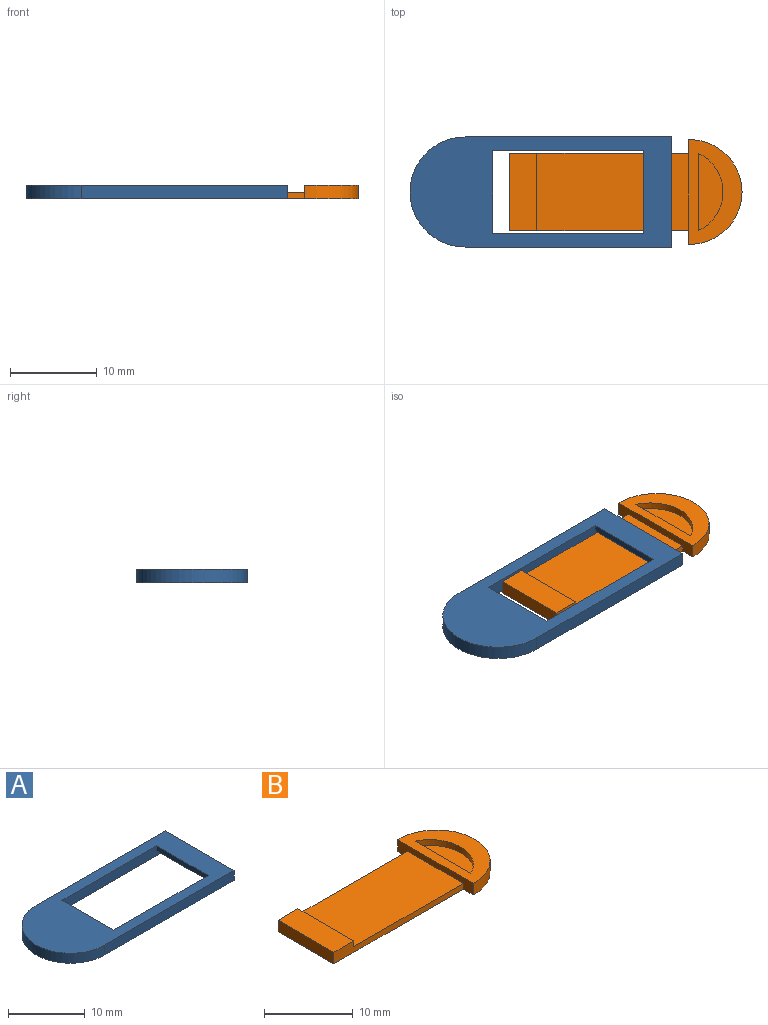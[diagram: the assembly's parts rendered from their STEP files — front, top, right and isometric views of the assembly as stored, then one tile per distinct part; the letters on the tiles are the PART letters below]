
ASSEMBLY  parts=2 mates=1
PART A: 11 faces, bbox 30.2x12.7x1.6 mm
  f0: plane 9.53x0.79mm, normal (-1,0,0), area 7.6mm2, adj f3,f7,f8,f10
  f1: plane 12.7x1.59mm, normal (1,0,0), area 12.6mm2, adj f3,f5,f6,f7,f8,f9,f10
  f2: plane 9.53x1.59mm, normal (1,0,0), area 15.1mm2, adj f3,f7,f8,f9
  f3: plane 20.64x1.59mm, normal (0,-1,0), area 30.2mm2, adj f0,f1,f2,f8,f9,f10
  f4: cylinder r=6.35mm len=12.7mm, axis (0,0,-1), area 31.7mm2, adj f5,f6,f8,f9
  f5: plane 23.81x1.59mm, normal (0,-1,0), area 37.8mm2, adj f1,f4,f8,f9
  f6: plane 23.81x1.59mm, normal (0,1,0), area 37.8mm2, adj f1,f4,f8,f9
  f7: plane 20.64x1.59mm, normal (0,1,0), area 30.2mm2, adj f0,f1,f2,f8,f9,f10
  f8: plane 30.16x12.7mm, normal (0,0,1), area 199.4mm2, adj f0,f1,f2,f3,f4,f5,f6,f7
  f9: plane 30.16x12.7mm, normal (0,0,-1), area 169.2mm2, adj f1,f2,f3,f4,f5,f6,f7
  f10: plane 9.53x3.18mm, normal (0,0,-1), area 30.2mm2, adj f0,f1,f3,f7
PART B: 13 faces, bbox 26.8x12.1x1.6 mm
  f0: plane 20.64x1.59mm, normal (0,1,0), area 18.9mm2, adj f1,f3,f6,f7,f11,f12
  f1: plane 8.89x3.18mm, normal (0,0,1), area 28.2mm2, adj f0,f3,f4,f11
  f2: plane 12.07x6.21mm, normal (0,0,1), area 41.3mm2, adj f5,f6,f8,f9
  f3: plane 8.89x1.59mm, normal (-1,0,0), area 14.1mm2, adj f0,f1,f4,f7
  f4: plane 20.64x1.59mm, normal (0,-1,0), area 18.9mm2, adj f1,f3,f6,f7,f11,f12
  f5: cylinder r=6.03mm len=12.07mm, axis (0,0,-1), area 30.6mm2, adj f2,f6,f7
  f6: plane 12.07x1.59mm, normal (-1,0,0), area 12.1mm2, adj f0,f2,f4,f5,f7,f12
  f7: plane 26.84x12.07mm, normal (0,0,-1), area 242.7mm2, adj f0,f3,f4,f5,f6
  f8: cylinder r=4.91mm len=8.89mm, axis (0,0,1), area 8.8mm2, adj f2,f9,f10
  f9: plane 8.89x0.79mm, normal (1,0,0), area 7.1mm2, adj f2,f8,f10
  f10: plane 8.89x2.82mm, normal (0,0,1), area 18mm2, adj f8,f9
  f11: plane 8.89x0.79mm, normal (1,0,0), area 7.1mm2, adj f0,f1,f4,f12
  f12: plane 17.46x8.89mm, normal (0,0,1), area 155.2mm2, adj f0,f4,f6,f11
PLACE A t=(7.12,7.36,-4.85)mm
PLACE B t=(12.25,6.74,-4.85)mm
MATE slider A.f2 <-> B.f3  axis (1,0,0) through (10.29,13.71,-4.06)mm
